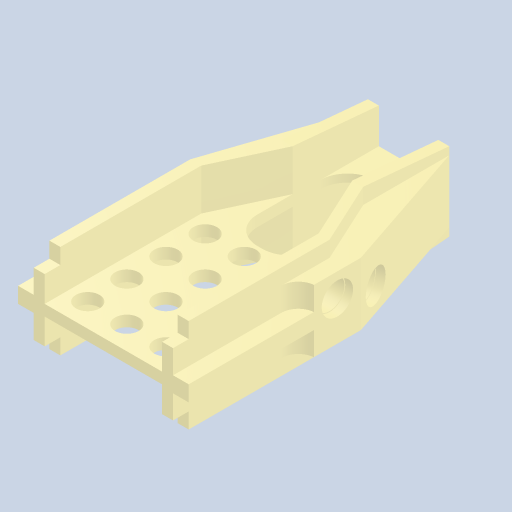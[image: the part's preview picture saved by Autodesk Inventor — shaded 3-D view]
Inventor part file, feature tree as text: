
AUTODESK INVENTOR PART (.ipt)
format: ipt  version: 2023 (Build 270158000, 158)  size: 411,648 bytes
history: native  units: mm
features: extrude x12, other x6, fillet x2, mirror x2, pattern_linear x1, pattern_circular x1
ambient origin geometry x8: Origin, YZ Plane, XZ Plane, XY Plane, X Axis, Y Axis, Z Axis, Center Point
bodies: Solid1 (feature_tree)
feature tree (24):
  other  "Sk:Base"
  extrude  "Ex:Midline"  Depth=3.75mm
  extrude  "Ex:FrontSupport"  Depth=10.0mm
  extrude  "Ex:SideRidge"  TaperAngle=0.0deg  [1 undecoded]
  extrude  "Ex:SideWall"  Depth=1.9mm
  extrude  "Ex:BaseHole"  TaperAngle=0.0deg  [1 undecoded]
  pattern_linear  "Pat:BaseHoles"  Spacing1=0.0mm  [1 undecoded]
  fillet  "Fillet:Support"  Radius=3.0mm
  extrude  "Ex:Widening"  Depth=0.7mm
  fillet  "Fillet:Side"  Radius=5.0mm
  extrude  "Ex:FrontTaper"  Depth=4.0mm
  extrude  "Ex:LidNotch"  Depth=1.5mm
  mirror  "Mirror1"
  mirror  "Mirror2"
  other  "Sk:ThreadHole1"
  other  "Sk:ThreadHole2"
  extrude  "Ex:ThreadHole1"  Depth=1.5mm
  extrude  "Ex:ThreadEntry1"  Depth=5.3mm TaperAngle=0.0deg
  extrude  "Ex:ThreadHole2"  Depth=2.5mm
  extrude  "Ex:ThreadEntry2"  Depth=2.5mm
  pattern_circular  "Pat:Threads"  [2 undecoded]
  other  "Sk:BaseHole"
  other  "Sk:FrontTaper"
  other  "Sk:LidNotch"
note: 5 required parameter values undecoded (feature->parameter linkage not recoverable at this tier; creation-order binding heuristic only, values carry confidence <= 0.55)
